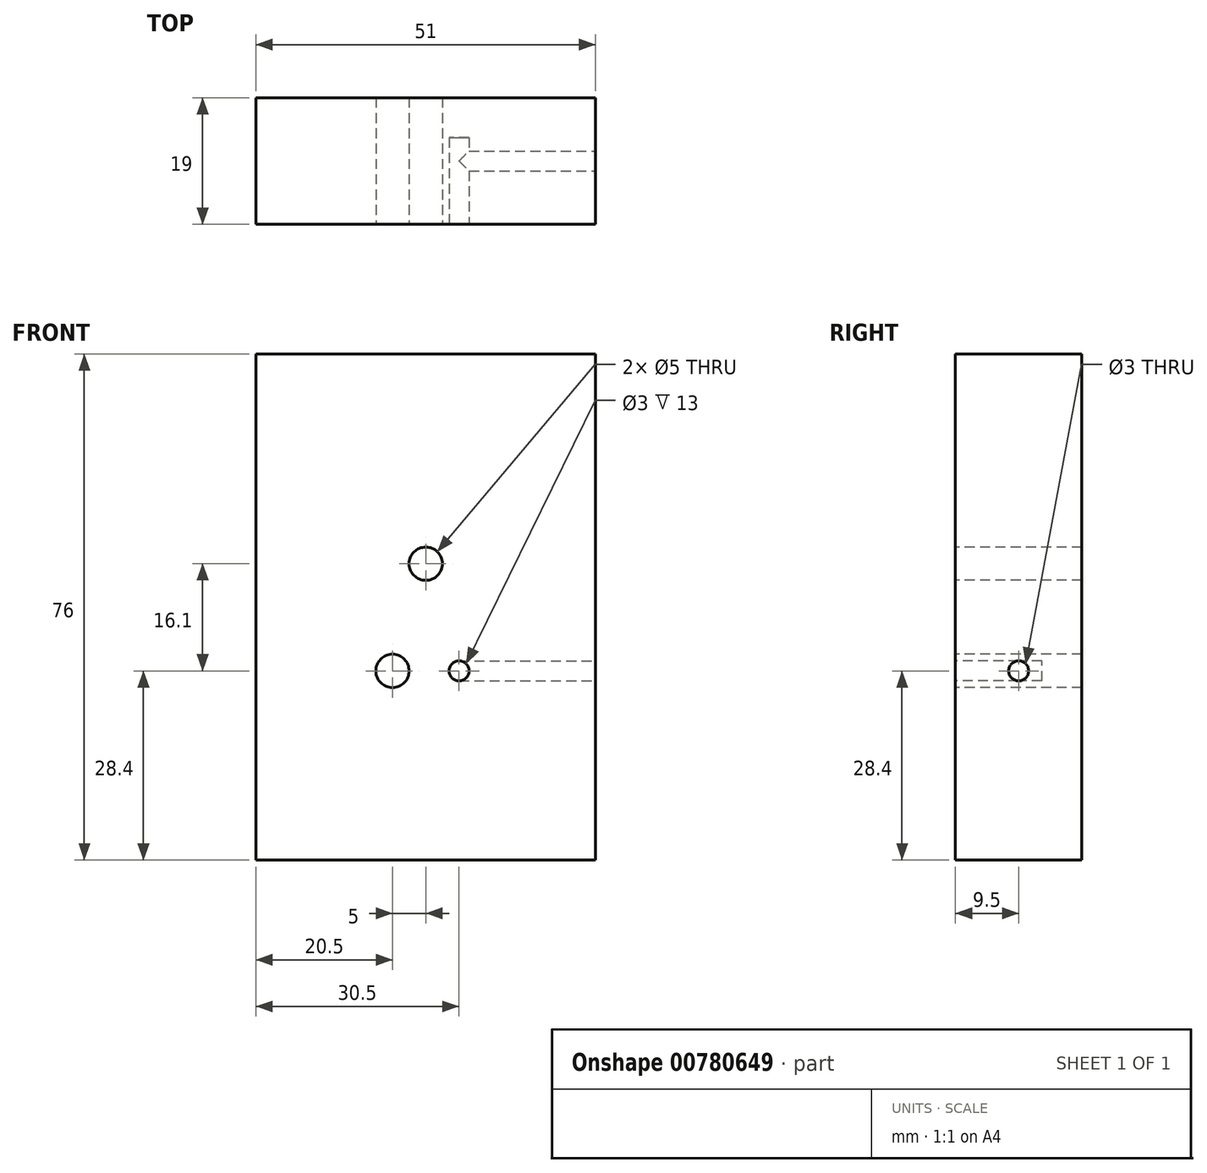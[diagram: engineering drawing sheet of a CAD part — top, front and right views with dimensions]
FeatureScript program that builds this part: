
annotation { "Feature Type Name" : "Feature", "Feature Type Description" : "" }
export const myFeature = defineFeature(function(context is Context, id is Id, definition is map)
    precondition{}
    {
        {
            var Q0;
            Q0=qCreatedBy(makeId("Front.planeOp"),FACE);
            var sketch = newSketch(context, id + "F0", { "sketchPlane" : qUnion([Q0])});
            skLineSegment(sketch, "E0.bottom", {"start": v(25.5, -38) * mm, "end": v(-25.5, -38) * mm});
            skLineSegment(sketch, "E0.top", {"start": v(25.5, 38) * mm, "end": v(-25.5, 38) * mm});
            skLineSegment(sketch, "E0.left", {"start": v(25.5, -38) * mm, "end": v(25.5, 38) * mm});
            skLineSegment(sketch, "E0.right", {"start": v(-25.5, -38) * mm, "end": v(-25.5, 38) * mm});
            skPoint(sketch, "E0.middle", {"position": v(0, 0) * mm});
            skSolve(sketch);
        }
        {
            var Q0;
            Q0 = qSketchRegion(id + "F0", true);
            extrude(context, id + "F1", {"entities" : qUnion([Q0]), "endBound" : BoundingType.SYMMETRIC, "depth" : 19 * mm, "offsetDistance" : 25 * mm});
        }
        {
            var Q0;
            Q0=makeQuery(id+"F1.opExtrude","CAP_FACE",FACE,{"disambiguationData":[OSD([sQuery(id+"F0.wireOp",EDGE,"E0.bottom"),sQuery(id+"F0.wireOp",EDGE,"E0.top"),sQuery(id+"F0.wireOp",EDGE,"E0.left"),sQuery(id+"F0.wireOp",EDGE,"E0.right")])],"isStart":false});
            var sketch = newSketch(context, id + "F2", { "sketchPlane" : qUnion([Q0])});
            skLineSegment(sketch, "E1", {"start": v(0, 0) * mm, "end": v(0, 6.5) * mm});
            skLineSegment(sketch, "E2", {"start": v(0, 0) * mm, "end": v(0, -9.6) * mm});
            skLineSegment(sketch, "E3", {"start": v(0, -9.6) * mm, "end": v(-5, -9.6) * mm});
            skLineSegment(sketch, "E4", {"start": v(0, -9.6) * mm, "end": v(5, -9.6) * mm});
            skCircle(sketch, "E5", {"center": v(0, 6.5) * mm, "radius": 2.5 * mm});
            skCircle(sketch, "E6", {"center": v(-5, -9.6) * mm, "radius": 2.5 * mm});
            skCircle(sketch, "E7", {"center": v(5, -9.6) * mm, "radius": 1.5 * mm});
            skSolve(sketch);
        }
        {
            var Q0;
            Q0=makeQuery(id+"F2.imprint","IMPRINT",FACE,{"disambiguationData":[TD([[makeQuery(id+"F2.imprint","IMPRINT",EDGE,{"derivedFrom":sQuery(id+"F2.wireOp",EDGE,"E5")}),1.0]])]});
            extrude(context, id + "F3", {"entities" : qUnion([Q0]), "operationType" : NewBodyOperationType.REMOVE, "endBound" : BoundingType.THROUGH_ALL, "oppositeDirection" : true, "depth" : 25 * mm, "offsetDistance" : 25 * mm});
        }
        {
            var Q0;
            Q0=makeQuery(id+"F2.imprint","IMPRINT",FACE,{"disambiguationData":[TD([[makeQuery(id+"F2.imprint","IMPRINT",EDGE,{"derivedFrom":sQuery(id+"F2.wireOp",EDGE,"E6")}),1.0]])]});
            extrude(context, id + "F4", {"entities" : qUnion([Q0]), "operationType" : NewBodyOperationType.REMOVE, "endBound" : BoundingType.THROUGH_ALL, "oppositeDirection" : true, "depth" : 25 * mm, "offsetDistance" : 25 * mm});
        }
        {
            var Q0;
            Q0=makeQuery(id+"F2.imprint","IMPRINT",FACE,{"disambiguationData":[TD([[makeQuery(id+"F2.imprint","IMPRINT",EDGE,{"derivedFrom":sQuery(id+"F2.wireOp",EDGE,"E7")}),1.0]])]});
            extrude(context, id + "F5", {"entities" : qUnion([Q0]), "operationType" : NewBodyOperationType.REMOVE, "oppositeDirection" : true, "depth" : 13 * mm, "offsetDistance" : 25 * mm});
        }
        {
            var Q0;
            Q0=makeQuery(id+"F1.opExtrude","SWEPT_FACE",FACE,{"disambiguationData":[OSD([sQuery(id+"F0.wireOp",EDGE,"E0.left")])]});
            var sketch = newSketch(context, id + "F6", { "sketchPlane" : qUnion([Q0])});
            skLineSegment(sketch, "E8", {"start": v(0, 0) * mm, "end": v(0, -9.6) * mm});
            skCircle(sketch, "E9", {"center": v(0, -9.6) * mm, "radius": 1.5 * mm});
            skSolve(sketch);
        }
        {
            var Q0;
            Q0 = qSketchRegion(id + "F6", true);
            extrude(context, id + "F7", {"entities" : qUnion([Q0]), "operationType" : NewBodyOperationType.REMOVE, "oppositeDirection" : true, "depth" : 20.5 * mm, "offsetDistance" : 25 * mm});
        }
    });
